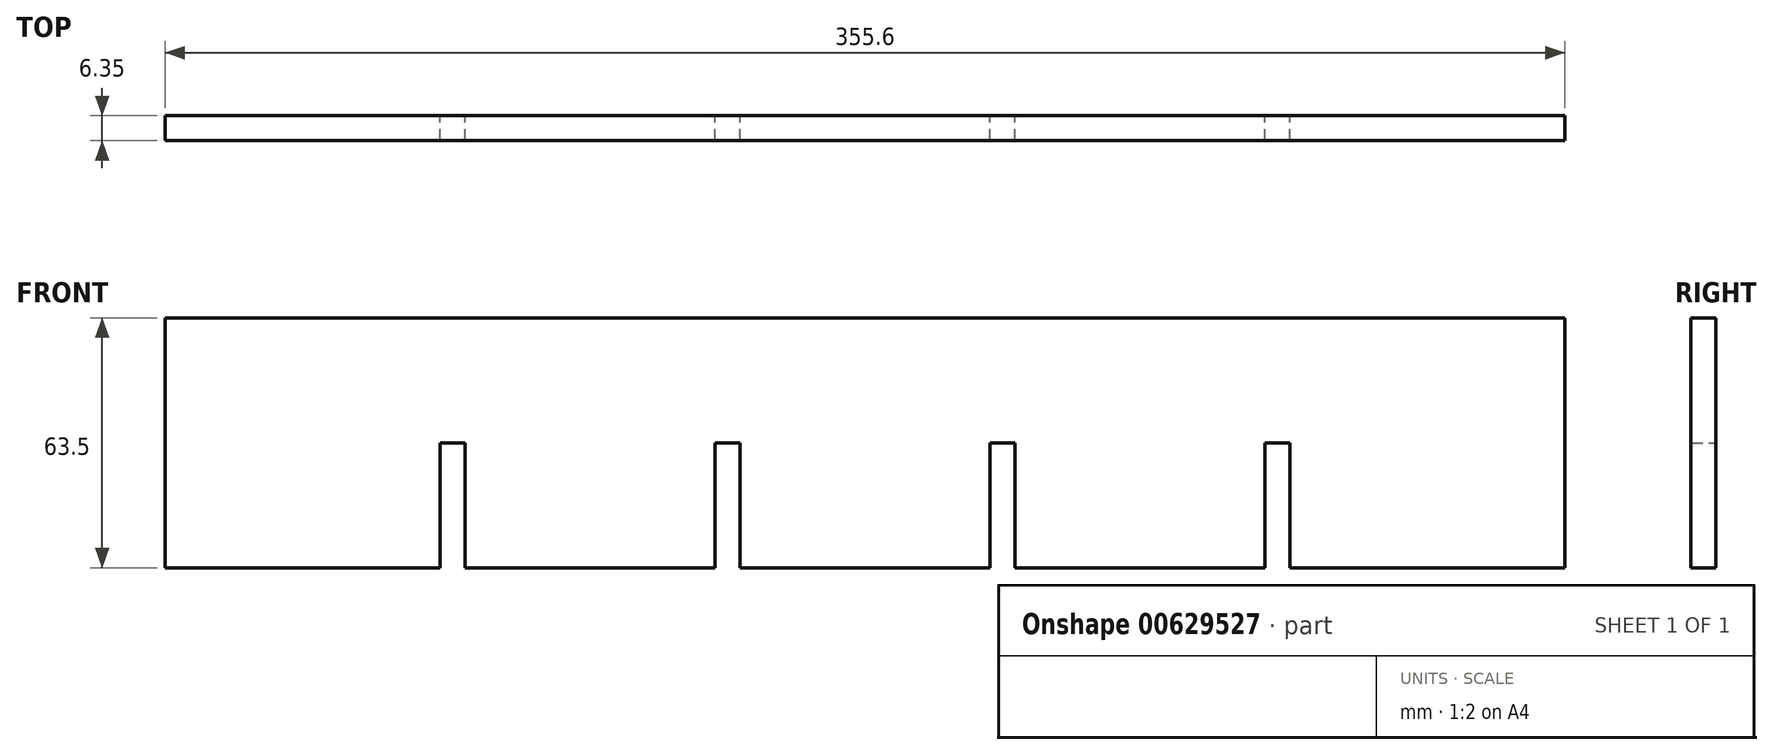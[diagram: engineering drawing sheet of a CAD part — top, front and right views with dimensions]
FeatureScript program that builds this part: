
annotation { "Feature Type Name" : "Feature", "Feature Type Description" : "" }
export const myFeature = defineFeature(function(context is Context, id is Id, definition is map)
    precondition{}
    {
        {
            var Q0;
            Q0=qCreatedBy(makeId("Front.planeOp"),FACE);
            var sketch = newSketch(context, id + "F0", { "sketchPlane" : qUnion([Q0])});
            skLineSegment(sketch, "E0", {"start": v(-177.8, 63.5) * mm, "end": v(177.8, 63.5) * mm});
            skLineSegment(sketch, "E1", {"start": v(177.8, 63.5) * mm, "end": v(177.8, 0) * mm});
            skLineSegment(sketch, "E2", {"start": v(177.8, 0) * mm, "end": v(107.95, 0) * mm});
            skLineSegment(sketch, "E3", {"start": v(107.95, 0) * mm, "end": v(107.95, 31.75) * mm});
            skLineSegment(sketch, "E4", {"start": v(107.95, 31.75) * mm, "end": v(101.6, 31.75) * mm});
            skLineSegment(sketch, "E5", {"start": v(101.6, 31.75) * mm, "end": v(101.6, 0) * mm});
            skLineSegment(sketch, "E6", {"start": v(101.6, 0) * mm, "end": v(38.1, 0) * mm});
            skLineSegment(sketch, "E7", {"start": v(38.1, 0) * mm, "end": v(38.1, 31.75) * mm});
            skLineSegment(sketch, "E8", {"start": v(38.1, 31.75) * mm, "end": v(31.75, 31.75) * mm});
            skLineSegment(sketch, "E9", {"start": v(31.75, 31.75) * mm, "end": v(31.75, 0) * mm});
            skLineSegment(sketch, "E10", {"start": v(31.75, 0) * mm, "end": v(-31.75, 0) * mm});
            skLineSegment(sketch, "E11", {"start": v(-31.75, 0) * mm, "end": v(-31.75, 31.75) * mm});
            skLineSegment(sketch, "E12", {"start": v(-31.75, 31.75) * mm, "end": v(-38.1, 31.75) * mm});
            skLineSegment(sketch, "E13", {"start": v(-38.1, 31.75) * mm, "end": v(-38.1, 0) * mm});
            skLineSegment(sketch, "E14", {"start": v(-38.1, 0) * mm, "end": v(-101.6, 0) * mm});
            skLineSegment(sketch, "E15", {"start": v(-101.6, 0) * mm, "end": v(-101.6, 31.75) * mm});
            skLineSegment(sketch, "E16", {"start": v(-101.6, 31.75) * mm, "end": v(-107.95, 31.75) * mm});
            skLineSegment(sketch, "E17", {"start": v(-107.95, 31.75) * mm, "end": v(-107.95, 0) * mm});
            skLineSegment(sketch, "E18", {"start": v(-107.95, 0) * mm, "end": v(-177.8, 0) * mm});
            skLineSegment(sketch, "E19", {"start": v(-177.8, 0) * mm, "end": v(-177.8, 63.5) * mm});
            skSolve(sketch);
        }
        {
            var Q0;
            Q0 = qSketchRegion(id + "F0", true);
            extrude(context, id + "F1", {"entities" : qUnion([Q0]), "depth" : 6.35 * mm, "offsetDistance" : 25.4 * mm});
        }
    });
